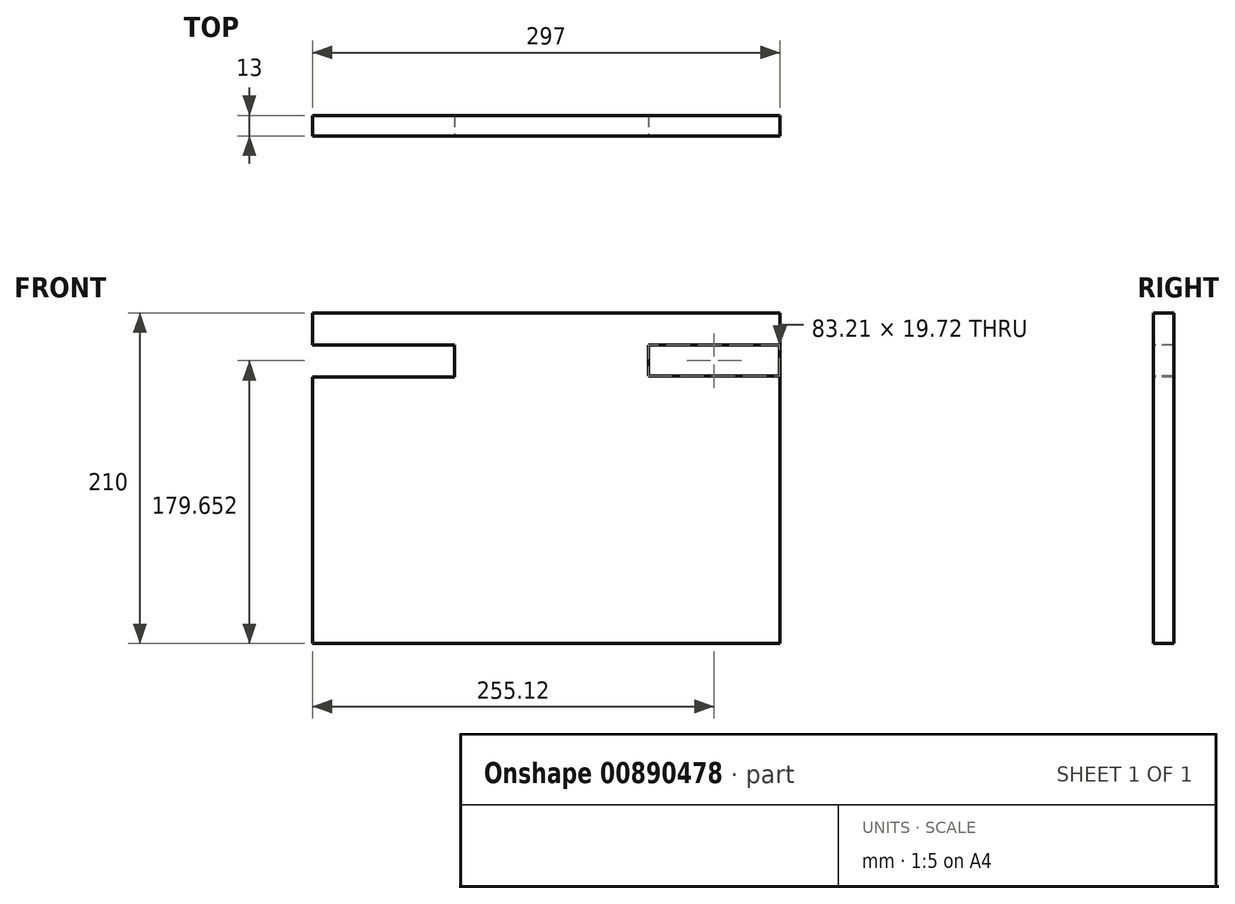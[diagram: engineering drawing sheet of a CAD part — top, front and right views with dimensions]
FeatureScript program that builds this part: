
annotation { "Feature Type Name" : "Feature", "Feature Type Description" : "" }
export const myFeature = defineFeature(function(context is Context, id is Id, definition is map)
    precondition{}
    {
        {
            var Q0;
            Q0=qCreatedBy(makeId("Front.planeOp"),FACE);
            var sketch = newSketch(context, id + "F0", { "sketchPlane" : qUnion([Q0])});
            skLineSegment(sketch, "E0.bottom", {"start": v(-148.98, 100.33) * mm, "end": v(148.02, 100.33) * mm});
            skLineSegment(sketch, "E0.top", {"start": v(-148.98, -109.67) * mm, "end": v(148.02, -109.67) * mm});
            skLineSegment(sketch, "E0.left", {"start": v(-148.98, 100.33) * mm, "end": v(-148.98, -109.67) * mm});
            skLineSegment(sketch, "E0.right", {"start": v(148.02, 100.33) * mm, "end": v(148.02, -109.67) * mm});
            skSolve(sketch);
        }
        {
            var Q0;
            Q0 = qSketchRegion(id + "F0", true);
            extrude(context, id + "F1", {"entities" : qUnion([Q0]), "depth" : 13 * mm, "offsetDistance" : 25 * mm});
        }
        {
            var Q0;
            Q0=makeQuery(id+"F1.opExtrude","CAP_FACE",FACE,{"disambiguationData":[OSD([sQuery(id+"F0.wireOp",EDGE,"E0.bottom"),sQuery(id+"F0.wireOp",EDGE,"E0.top"),sQuery(id+"F0.wireOp",EDGE,"E0.left"),sQuery(id+"F0.wireOp",EDGE,"E0.right")])],"isStart":false});
            var sketch = newSketch(context, id + "F2", { "sketchPlane" : qUnion([Q0])});
            skLineSegment(sketch, "E1.bottom", {"start": v(-148.98, 79.84) * mm, "end": v(-58.76, 79.84) * mm});
            skLineSegment(sketch, "E1.top", {"start": v(-148.98, 59.59) * mm, "end": v(-58.76, 59.59) * mm});
            skLineSegment(sketch, "E1.left", {"start": v(-148.98, 79.84) * mm, "end": v(-148.98, 59.59) * mm});
            skLineSegment(sketch, "E1.right", {"start": v(-58.76, 79.84) * mm, "end": v(-58.76, 59.59) * mm});
            skSolve(sketch);
        }
        {
            var Q0;
            Q0=makeQuery(id+"F2.imprint","IMPRINT",FACE,{"disambiguationData":[TD([[makeQuery(id+"F2.imprint","IMPRINT",EDGE,{"derivedFrom":sQuery(id+"F2.wireOp",EDGE,"E1.bottom")}),-1.0]])]});
            extrude(context, id + "F3", {"entities" : qUnion([Q0]), "operationType" : NewBodyOperationType.REMOVE, "oppositeDirection" : true, "depth" : 25 * mm, "offsetDistance" : 25 * mm});
        }
        {
            var Q0;
            Q0=makeQuery(id+"F1.opExtrude","CAP_FACE",FACE,{"disambiguationData":[OSD([sQuery(id+"F0.wireOp",EDGE,"E0.bottom"),sQuery(id+"F0.wireOp",EDGE,"E0.top"),sQuery(id+"F0.wireOp",EDGE,"E0.left"),sQuery(id+"F0.wireOp",EDGE,"E0.right")])],"isStart":false});
            var sketch = newSketch(context, id + "F4", { "sketchPlane" : qUnion([Q0])});
            skLineSegment(sketch, "E2.bottom", {"start": v(64.53, 79.84) * mm, "end": v(147.75, 79.84) * mm});
            skLineSegment(sketch, "E2.top", {"start": v(64.53, 60.12) * mm, "end": v(147.75, 60.12) * mm});
            skLineSegment(sketch, "E2.left", {"start": v(64.53, 79.84) * mm, "end": v(64.53, 60.12) * mm});
            skLineSegment(sketch, "E2.right", {"start": v(147.75, 79.84) * mm, "end": v(147.75, 60.12) * mm});
            skSolve(sketch);
        }
        {
            var Q0;
            Q0=makeQuery(id+"F4.imprint","IMPRINT",FACE,{"disambiguationData":[TD([[makeQuery(id+"F4.imprint","IMPRINT",EDGE,{"derivedFrom":sQuery(id+"F4.wireOp",EDGE,"E2.bottom")}),-1.0]])]});
            extrude(context, id + "F5", {"entities" : qUnion([Q0]), "operationType" : NewBodyOperationType.REMOVE, "oppositeDirection" : true, "depth" : 25 * mm, "offsetDistance" : 25 * mm});
        }
    });
